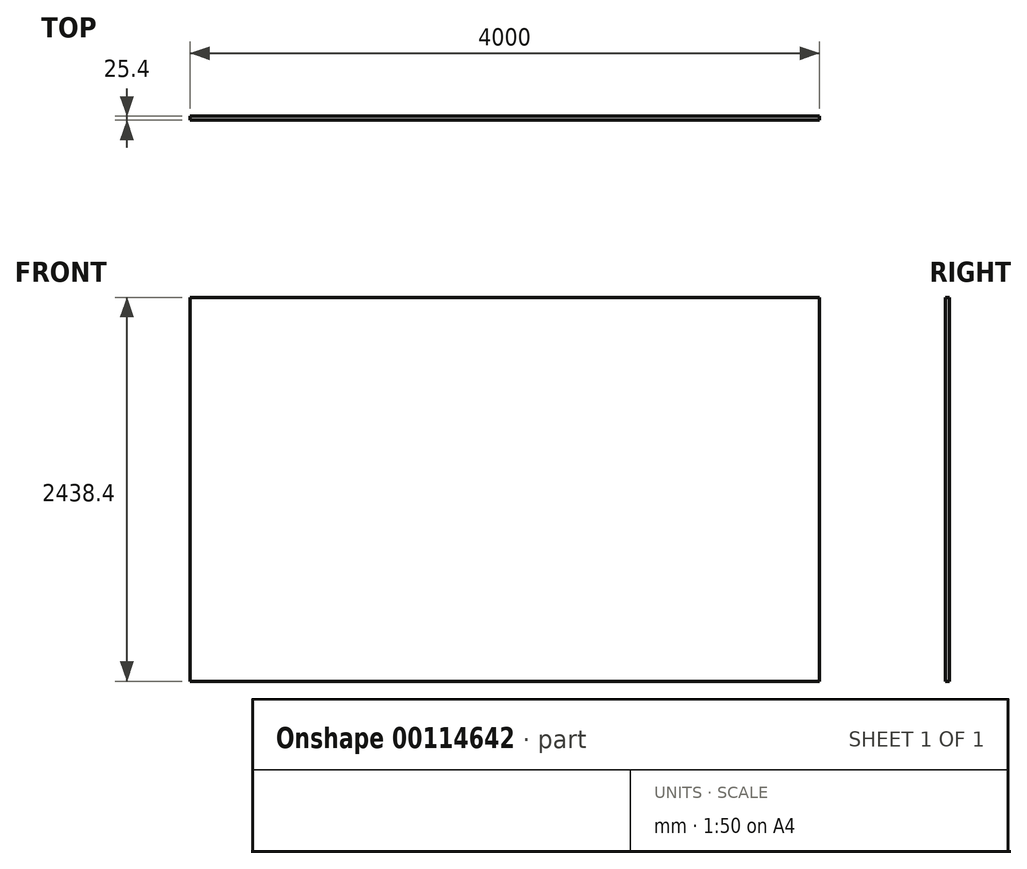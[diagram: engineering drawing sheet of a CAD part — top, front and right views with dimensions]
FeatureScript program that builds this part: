
annotation { "Feature Type Name" : "Feature", "Feature Type Description" : "" }
export const myFeature = defineFeature(function(context is Context, id is Id, definition is map)
    precondition{}
    {
        {
            var Q0;
            Q0=qCreatedBy(makeId("Front.planeOp"),FACE);
            var sketch = newSketch(context, id + "F0", { "sketchPlane" : qUnion([Q0])});
            skLineSegment(sketch, "E0.bottom", {"start": v(2000, 1219.2) * mm, "end": v(-2000, 1219.2) * mm});
            skLineSegment(sketch, "E0.top", {"start": v(2000, -1219.2) * mm, "end": v(-2000, -1219.2) * mm});
            skLineSegment(sketch, "E0.left", {"start": v(2000, 1219.2) * mm, "end": v(2000, -1219.2) * mm});
            skLineSegment(sketch, "E0.right", {"start": v(-2000, 1219.2) * mm, "end": v(-2000, -1219.2) * mm});
            skPoint(sketch, "E0.middle", {"position": v(0, 0) * mm});
            skSolve(sketch);
        }
        {
            var Q0;
            Q0=makeQuery(id+"F0.imprint","IMPRINT",FACE,{"disambiguationData":[TD([[makeQuery(id+"F0.imprint","IMPRINT",EDGE,{"derivedFrom":sQuery(id+"F0.wireOp",EDGE,"E0.bottom")}),1.0]])]});
            extrude(context, id + "F1", {"entities" : qUnion([Q0]), "depth" : 25.4 * mm});
        }
    });
